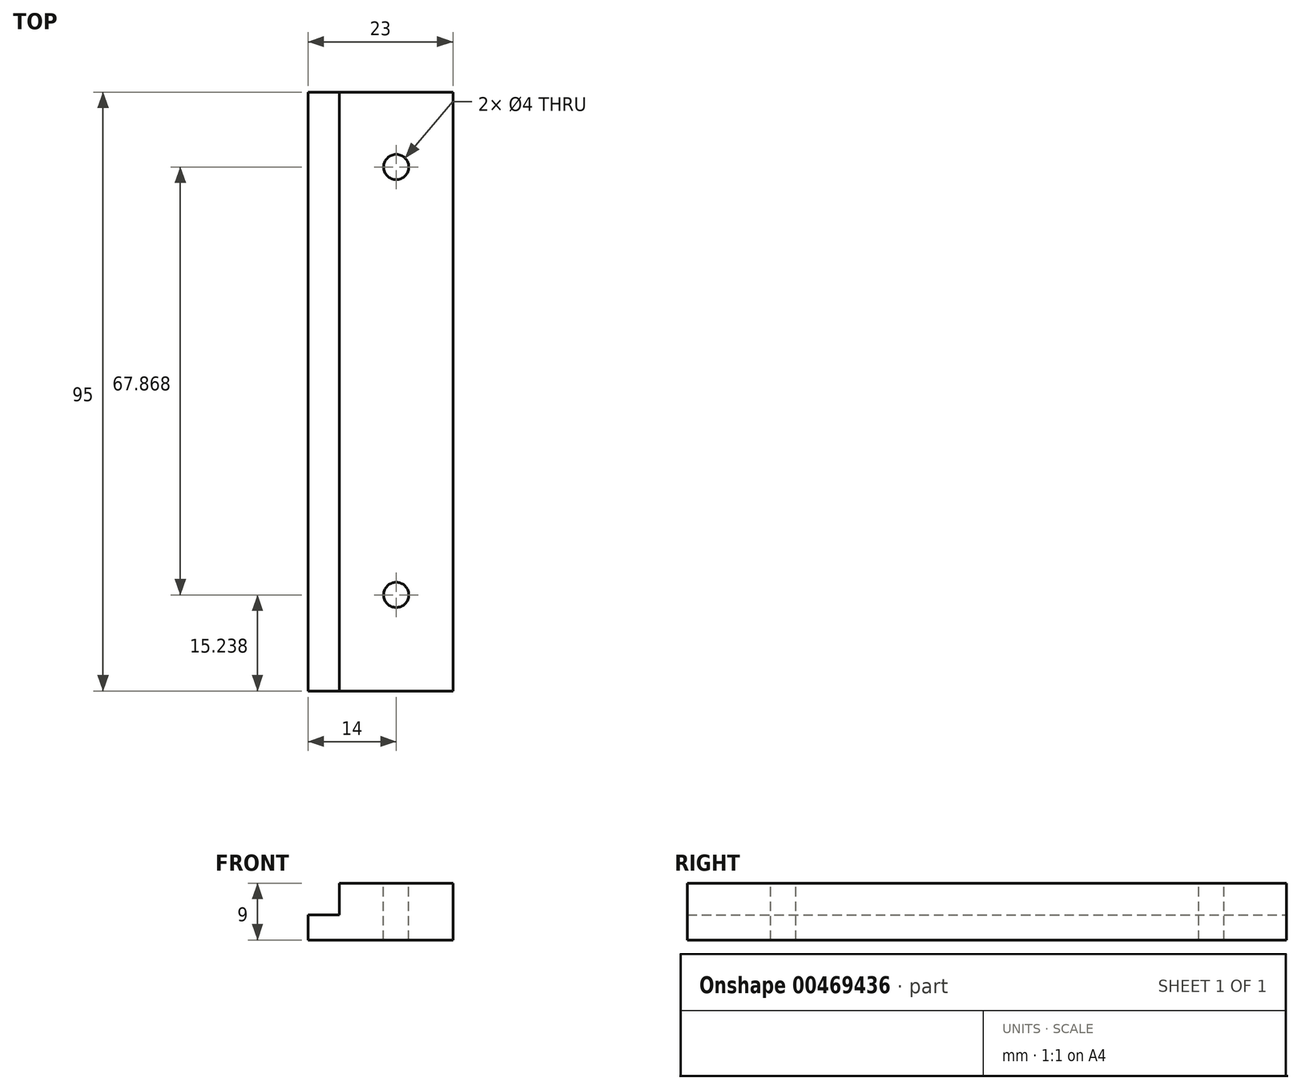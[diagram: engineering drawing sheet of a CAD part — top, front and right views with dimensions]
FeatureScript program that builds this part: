
annotation { "Feature Type Name" : "Feature", "Feature Type Description" : "" }
export const myFeature = defineFeature(function(context is Context, id is Id, definition is map)
    precondition{}
    {
        {
            var Q0;
            Q0=qCreatedBy(makeId("Top.planeOp"),FACE);
            var sketch = newSketch(context, id + "F0", { "sketchPlane" : qUnion([Q0])});
            skLineSegment(sketch, "E0.bottom", {"start": v(11.5, -47.5) * mm, "end": v(-11.5, -47.5) * mm});
            skLineSegment(sketch, "E0.top", {"start": v(11.5, 47.5) * mm, "end": v(-11.5, 47.5) * mm});
            skLineSegment(sketch, "E0.left", {"start": v(11.5, -47.5) * mm, "end": v(11.5, 47.5) * mm});
            skLineSegment(sketch, "E0.right", {"start": v(-11.5, -47.5) * mm, "end": v(-11.5, 47.5) * mm});
            skPoint(sketch, "E0.middle", {"position": v(0, 0) * mm});
            skSolve(sketch);
        }
        {
            var Q0;
            Q0 = qSketchRegion(id + "F0", true);
            extrude(context, id + "F1", {"entities" : qUnion([Q0]), "depth" : 9 * mm});
        }
        {
            var Q0;
            Q0=makeQuery(id+"F1.opExtrude","CAP_FACE",FACE,{"disambiguationData":[OSD([sQuery(id+"F0.wireOp",EDGE,"E0.bottom"),sQuery(id+"F0.wireOp",EDGE,"E0.top"),sQuery(id+"F0.wireOp",EDGE,"E0.left"),sQuery(id+"F0.wireOp",EDGE,"E0.right")])],"isStart":false});
            var sketch = newSketch(context, id + "F2", { "sketchPlane" : qUnion([Q0])});
            skLineSegment(sketch, "E1.bottom", {"start": v(-11.5, 47.5) * mm, "end": v(-6.5, 47.5) * mm});
            skLineSegment(sketch, "E1.top", {"start": v(-11.5, -47.5) * mm, "end": v(-6.5, -47.5) * mm});
            skLineSegment(sketch, "E1.left", {"start": v(-11.5, 47.5) * mm, "end": v(-11.5, -47.5) * mm});
            skLineSegment(sketch, "E1.right", {"start": v(-6.5, 47.5) * mm, "end": v(-6.5, -47.5) * mm});
            skSolve(sketch);
        }
        {
            var Q0;
            Q0 = qSketchRegion(id + "F2", true);
            extrude(context, id + "F3", {"entities" : qUnion([Q0]), "operationType" : NewBodyOperationType.REMOVE, "oppositeDirection" : true, "depth" : 5 * mm});
        }
        {
            var Q0;
            Q0=makeQuery(id+"F1.opExtrude","CAP_FACE",FACE,{"disambiguationData":[OSD([sQuery(id+"F0.wireOp",EDGE,"E0.bottom"),sQuery(id+"F0.wireOp",EDGE,"E0.top"),sQuery(id+"F0.wireOp",EDGE,"E0.left"),sQuery(id+"F0.wireOp",EDGE,"E0.right")])],"isStart":false});
            var sketch = newSketch(context, id + "F4", { "sketchPlane" : qUnion([Q0])});
            skCircle(sketch, "E2", {"center": v(2.5, 35.6) * mm, "radius": 2 * mm});
            skPoint(sketch, "E2.centerSnap0", {"position": v(2.5, 47.5) * mm});
            skCircle(sketch, "E3", {"center": v(2.5, -32.26) * mm, "radius": 2 * mm});
            skSolve(sketch);
        }
        {
            var Q0;
            Q0 = qSketchRegion(id + "F4", true);
            extrude(context, id + "F5", {"entities" : qUnion([Q0]), "operationType" : NewBodyOperationType.REMOVE, "oppositeDirection" : true, "depth" : 12.45 * mm});
        }
    });
